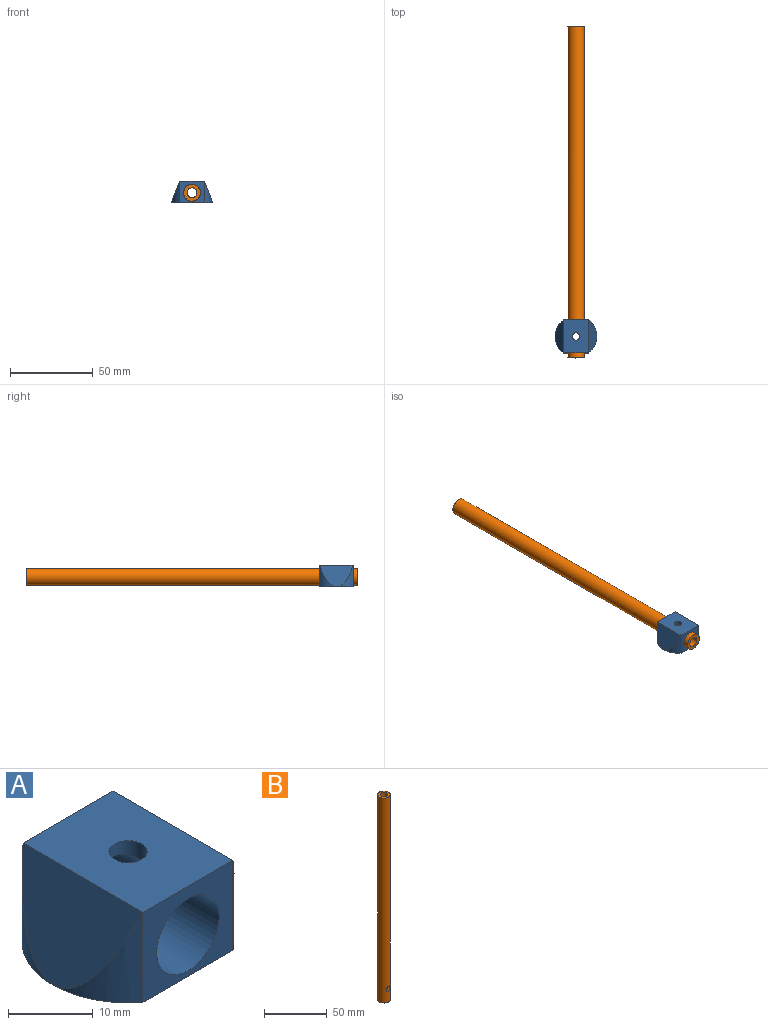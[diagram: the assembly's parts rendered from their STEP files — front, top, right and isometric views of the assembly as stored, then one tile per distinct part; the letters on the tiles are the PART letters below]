
ASSEMBLY  parts=2 mates=1
PART A: 13 faces, bbox 25x20x13 mm
  f0: plane 15x13mm, normal (0,-1,0), area 110.1mm2, adj f1,f2,f3,f4,f5
  f1: cylinder r=12.5mm len=13mm, axis (0,0,-1), area 51.7mm2, adj f0,f2,f6
  f2: plane 25x20mm, normal (0,0,-1), area 423.9mm2, adj f0,f1,f4,f7,f8,f9,f10
  f3: plane 20x15mm, normal (0,0,1), area 284.1mm2, adj f0,f6,f9,f11,f12
  f4: cylinder r=12.5mm len=13mm, axis (0,0,-1), area 51.7mm2, adj f0,f2,f11
  f5: cylinder r=5.2mm len=20mm, axis (0,-1,0), area 620.9mm2, adj f0,f9,f10,f12
  f6: plane 20x13mm, normal (0.93,0,0.36), area 194.7mm2, adj f1,f3,f7
  f7: cylinder r=12.5mm len=13mm, axis (0,0,-1), area 51.7mm2, adj f2,f6,f9
  f8: cylinder r=12.5mm len=13mm, axis (0,0,-1), area 51.7mm2, adj f2,f9,f11
  f9: plane 15x13mm, normal (0,1,0), area 110.1mm2, adj f2,f3,f5,f7,f8
  f10: cylinder r=2.25mm len=4.5mm, axis (0,0,1), area 14.9mm2, adj f2,f5
  f11: plane 20x13mm, normal (-0.93,0,0.36), area 194.7mm2, adj f3,f4,f8
  f12: cylinder r=2.25mm len=4.5mm, axis (0,0,1), area 29mm2, adj f3,f5
PART B: 6 faces, bbox 10x10x200 mm
  f0: cylinder r=3mm len=200mm, axis (0,0,-1), area 3735.2mm2, adj f2,f3,f4,f5
  f1: cylinder r=5mm len=200mm, axis (0,0,-1), area 6250.5mm2, adj f2,f3,f4,f5
  f2: plane 10x10mm, normal (0,0,1), area 50.3mm2, adj f0,f1
  f3: plane 10x10mm, normal (0,0,-1), area 50.3mm2, adj f0,f1
  f4: cylinder r=2.25mm len=4.5mm, axis (0,1,0), area 31.4mm2, adj f0,f1
  f5: cylinder r=2.25mm len=4.5mm, axis (0,1,0), area 31.4mm2, adj f0,f1
PLACE A t=(-1.26,1.93,-2.52)mm
PLACE B rot(axis=(-1,0,0),90deg) t=(-1.26,-11.07,3.49)mm
MATE fastened B.f4 <-> A.f1  axis (0,0,-1) through (-1.26,1.93,8.51)mm
